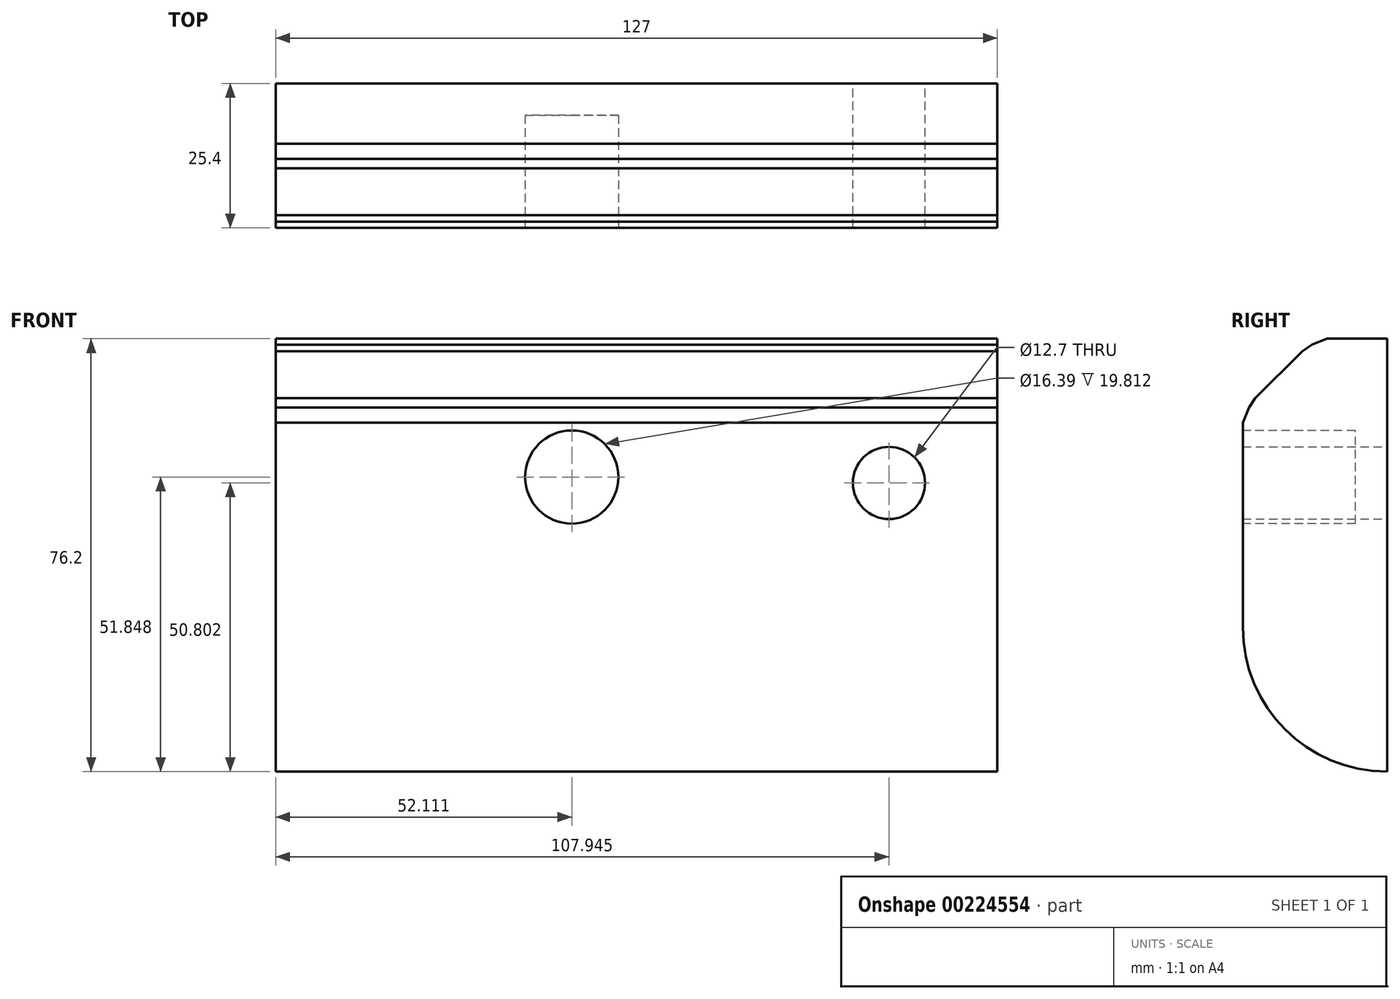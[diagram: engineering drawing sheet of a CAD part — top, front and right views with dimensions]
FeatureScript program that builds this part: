
annotation { "Feature Type Name" : "Feature", "Feature Type Description" : "" }
export const myFeature = defineFeature(function(context is Context, id is Id, definition is map)
    precondition{}
    {
        {
            var Q0;
            Q0=qCreatedBy(makeId("Front.planeOp"),FACE);
            var sketch = newSketch(context, id + "F0", { "sketchPlane" : qUnion([Q0])});
            skLineSegment(sketch, "E0.bottom", {"start": v(-32.8, 54.52) * mm, "end": v(94.2, 54.52) * mm});
            skLineSegment(sketch, "E0.top", {"start": v(-32.8, -21.68) * mm, "end": v(94.2, -21.68) * mm});
            skLineSegment(sketch, "E0.left", {"start": v(-32.8, 54.52) * mm, "end": v(-32.8, -21.68) * mm});
            skLineSegment(sketch, "E0.right", {"start": v(94.2, 54.52) * mm, "end": v(94.2, -21.68) * mm});
            skCircle(sketch, "E1", {"center": v(75.16, 29.12) * mm, "radius": 6.35 * mm});
            skSolve(sketch);
        }
        {
            var Q0;
            Q0 = qSketchRegion(id + "F0", true);
            extrude(context, id + "F1", {"entities" : qUnion([Q0]), "depth" : 25.4 * mm});
        }
        {
            var Q0;
            Q0=makeQuery(id+"F1.opExtrude","CAP_FACE",FACE,{"disambiguationData":[OSD([sQuery(id+"F0.wireOp",EDGE,"E0.bottom"),sQuery(id+"F0.wireOp",EDGE,"E0.top"),sQuery(id+"F0.wireOp",EDGE,"E0.left"),sQuery(id+"F0.wireOp",EDGE,"E0.right"),sQuery(id+"F0.wireOp",EDGE,"E1")])],"isStart":false});
            var sketch = newSketch(context, id + "F2", { "sketchPlane" : qUnion([Q0])});
            skCircle(sketch, "E2", {"center": v(19.32, 30.17) * mm, "radius": 8.2 * mm});
            skSolve(sketch);
        }
        {
            var Q0;
            Q0=makeQuery(id+"F2.imprint","IMPRINT",FACE,{"disambiguationData":[TD([[makeQuery(id+"F2.imprint","IMPRINT",EDGE,{"derivedFrom":sQuery(id+"F2.wireOp",EDGE,"E2")}),1.0]])]});
            extrude(context, id + "F3", {"entities" : qUnion([Q0]), "operationType" : NewBodyOperationType.REMOVE, "oppositeDirection" : true, "depth" : 19.8 * mm});
        }
        {
            var Q0;
            Q0=makeQuery(id+"F1.opExtrude","CAP_EDGE",EDGE,{"disambiguationData":[OSD([sQuery(id+"F0.wireOp",EDGE,"E0.bottom")])],"isStart":false});
            chamfer(context, id + "F4", {"entities" : qUnion([Q0]), "width" : 12.7 * mm, "tangentPropagation" : true});
        }
        {
            var Q0;
            {var subQ0=sQuery(id+"F0.wireOp",EDGE,"E0.bottom");Q0=makeQuery(id+"F4.opChamfer","BLEND_EDGE",EDGE,{"blendedFrom":[makeQuery(id+"F1.opExtrude","CAP_EDGE",EDGE,{"disambiguationData":[OSD([subQ0])],"isStart":false}),makeQuery(id+"F1.opExtrude","SWEPT_FACE",FACE,{"disambiguationData":[OSD([subQ0])]})],"blendedInto":[makeQuery(id+"F1.opExtrude","SWEPT_FACE",FACE,{"disambiguationData":[OSD([subQ0])]})]});}
            chamfer(context, id + "F5", {"entities" : qUnion([Q0]), "width" : 5.08 * mm, "tangentPropagation" : true});
        }
        {
            var Q0;
            {var subQ0=sQuery(id+"F0.wireOp",EDGE,"E0.bottom");Q0=makeQuery(id+"F4.opChamfer","BLEND_EDGE",EDGE,{"blendedFrom":[makeQuery(id+"F1.opExtrude","CAP_EDGE",EDGE,{"disambiguationData":[OSD([subQ0])],"isStart":false}),makeQuery(id+"F1.opExtrude","CAP_FACE",FACE,{"disambiguationData":[OSD([subQ0,sQuery(id+"F0.wireOp",EDGE,"E0.top"),sQuery(id+"F0.wireOp",EDGE,"E0.left"),sQuery(id+"F0.wireOp",EDGE,"E0.right"),sQuery(id+"F0.wireOp",EDGE,"E1")])],"isStart":false})],"blendedInto":[makeQuery(id+"F1.opExtrude","CAP_FACE",FACE,{"disambiguationData":[OSD([subQ0,sQuery(id+"F0.wireOp",EDGE,"E0.top"),sQuery(id+"F0.wireOp",EDGE,"E0.left"),sQuery(id+"F0.wireOp",EDGE,"E0.right"),sQuery(id+"F0.wireOp",EDGE,"E1")])],"isStart":false})]});}
            chamfer(context, id + "F6", {"entities" : qUnion([Q0]), "width" : 5.08 * mm, "tangentPropagation" : true});
        }
        {
            var Q0;
            {var subQ0=sQuery(id+"F0.wireOp",EDGE,"E0.bottom");Q0=makeQuery(id+"F6.opChamfer","BLEND_EDGE",EDGE,{"blendedFrom":[makeQuery(id+"F4.opChamfer","BLEND_EDGE",EDGE,{"blendedFrom":[makeQuery(id+"F1.opExtrude","CAP_EDGE",EDGE,{"disambiguationData":[OSD([subQ0])],"isStart":false}),makeQuery(id+"F1.opExtrude","CAP_FACE",FACE,{"disambiguationData":[OSD([subQ0,sQuery(id+"F0.wireOp",EDGE,"E0.top"),sQuery(id+"F0.wireOp",EDGE,"E0.left"),sQuery(id+"F0.wireOp",EDGE,"E0.right"),sQuery(id+"F0.wireOp",EDGE,"E1")])],"isStart":false})],"blendedInto":[makeQuery(id+"F1.opExtrude","CAP_FACE",FACE,{"disambiguationData":[OSD([subQ0,sQuery(id+"F0.wireOp",EDGE,"E0.top"),sQuery(id+"F0.wireOp",EDGE,"E0.left"),sQuery(id+"F0.wireOp",EDGE,"E0.right"),sQuery(id+"F0.wireOp",EDGE,"E1")])],"isStart":false})]}),makeQuery(id+"F4.opChamfer","BLEND_FACE",FACE,{"disambiguationData":[OSD([subQ0])]})],"blendedInto":[makeQuery(id+"F4.opChamfer","BLEND_FACE",FACE,{"disambiguationData":[OSD([subQ0])]})]});}
            chamfer(context, id + "F7", {"entities" : qUnion([Q0]), "width" : 5.08 * mm, "tangentPropagation" : true});
        }
        {
            var Q0;
            {var subQ0=sQuery(id+"F0.wireOp",EDGE,"E0.bottom");Q0=makeQuery(id+"F5.opChamfer","BLEND_EDGE",EDGE,{"blendedFrom":[makeQuery(id+"F4.opChamfer","BLEND_EDGE",EDGE,{"blendedFrom":[makeQuery(id+"F1.opExtrude","CAP_EDGE",EDGE,{"disambiguationData":[OSD([subQ0])],"isStart":false}),makeQuery(id+"F1.opExtrude","SWEPT_FACE",FACE,{"disambiguationData":[OSD([subQ0])]})],"blendedInto":[makeQuery(id+"F1.opExtrude","SWEPT_FACE",FACE,{"disambiguationData":[OSD([subQ0])]})]}),makeQuery(id+"F4.opChamfer","BLEND_FACE",FACE,{"disambiguationData":[OSD([subQ0])]})],"blendedInto":[makeQuery(id+"F4.opChamfer","BLEND_FACE",FACE,{"disambiguationData":[OSD([subQ0])]})]});}
            chamfer(context, id + "F8", {"entities" : qUnion([Q0]), "width" : 5.08 * mm, "tangentPropagation" : true});
        }
        {
            var Q0;
            Q0=makeQuery(id+"F1.opExtrude","CAP_EDGE",EDGE,{"disambiguationData":[OSD([sQuery(id+"F0.wireOp",EDGE,"E0.top")])],"isStart":false});
            fillet(context, id + "F9", {"entities" : qUnion([Q0]), "radius" : 25.4 * mm, "tangentPropagation" : true, "allowEdgeOverflow" : false});
        }
    });
